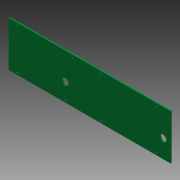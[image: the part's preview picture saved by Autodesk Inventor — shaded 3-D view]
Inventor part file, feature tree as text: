
AUTODESK INVENTOR PART (.ipt)
format: ipt  version: 2011 (Build 150239000, 239)  size: 104,448 bytes
history: native  units: mm (DEFAULTED — no unit token found)
features: sketch x3, hole x2, extrude x1
ambient origin geometry x8: Origin, YZ Plane, XZ Plane, XY Plane, X Axis, Y Axis, Z Axis, Center Point
bodies: Solid1 (feature_tree)
feature tree (6):
  extrude  "PCB"  Depth=76.2mm
  hole  "Hole1"  [1 undecoded]
  hole  "Hole2"  [1 undecoded]
  sketch  "Sketch1"  dims[d0=273.05mm d1=76.2mm]
  sketch  "Sketch2"  dims[d2=2.2098mm d3=0.0mm d4=67.8434mm]
  sketch  "Sketch3"  dims[d5=14.0208mm d6=93.0148mm d7=47.5742mm d8=94.488mm d9=81.534mm d10=3.429mm d11=12.7mm d12=9.525mm d13=6.35mm d14=14.3117mm d15=19.05mm d16=20.594885mm d17=165.1mm d18=26.2636mm d19=59.055mm d20=11.0744mm d21=12.7mm d22=9.525mm d23=6.35mm d24=14.3117mm d25=19.05mm d26=20.594885mm]
note: 2 required parameter values undecoded (feature->parameter linkage not recoverable at this tier; creation-order binding heuristic only, values carry confidence <= 0.55)
